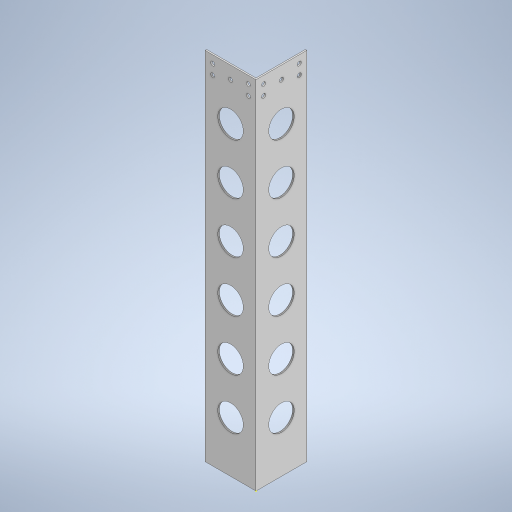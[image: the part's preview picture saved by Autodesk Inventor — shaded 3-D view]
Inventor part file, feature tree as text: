
AUTODESK INVENTOR PART (.ipt)
format: ipt  version: 2024 (Build 280153000, 153)  size: 326,144 bytes
history: native  units: mm
features: sketch x4, extrude x3
ambient origin geometry x8: Origin, YZ Plane, XZ Plane, XY Plane, X Axis, Y Axis, Z Axis, Center Point
bodies: Body1 (feature_tree)
feature tree (7):
  extrude  "Extrusión6"  Depth=100.0mm
  extrude  "Extrusión7"  Depth=700.0mm TaperAngle=0.0deg
  extrude  "Extrusión8"  Depth=50.0mm
  sketch  "Boceto9"  dims[d53=50.0mm d54=50.0mm d55=60.0mm d57=100.0mm d58=10.0mm d60=10.0mm d62=8.0mm d64=15.0mm d65=15.0mm d66=8.0mm d67=8.0mm d68=8.0mm d69=15.0mm d70=15.0mm d71=15.0mm d72=15.0mm d73=15.0mm d74=15.0mm d75=8.0mm d76=25.0mm d77=50.0mm d78=700.0mm d79=0.0mm d81=60.0mm d83=10.0mm d84=50.0mm d85=50.0mm d86=50.0mm d87=50.0mm d88=100.0mm d89=8.0mm d90=15.0mm d91=15.0mm d92=8.0mm d93=8.0mm d94=8.0mm d95=15.0mm d96=15.0mm d97=15.0mm d98=15.0mm d99=15.0mm d100=15.0mm d101=8.0mm d102=25.0mm d103=50.0mm d104=10.0mm d105=0.0mm d106=0.0mm d107=0.0mm d108=700.0mm d109=0.0mm d110=0.0mm d2=0.5mm d3=0.872665mm d4=0.5mm d5=0.872665mm]
  sketch  "Boceto6"  dims[d46=100.0mm d47=100.0mm]
  sketch  "Boceto7"  dims[d48=3.0mm d49=700.0mm d50=0.0mm]
  sketch  "Boceto8"  dims[d51=50.0mm d52=50.0mm]
